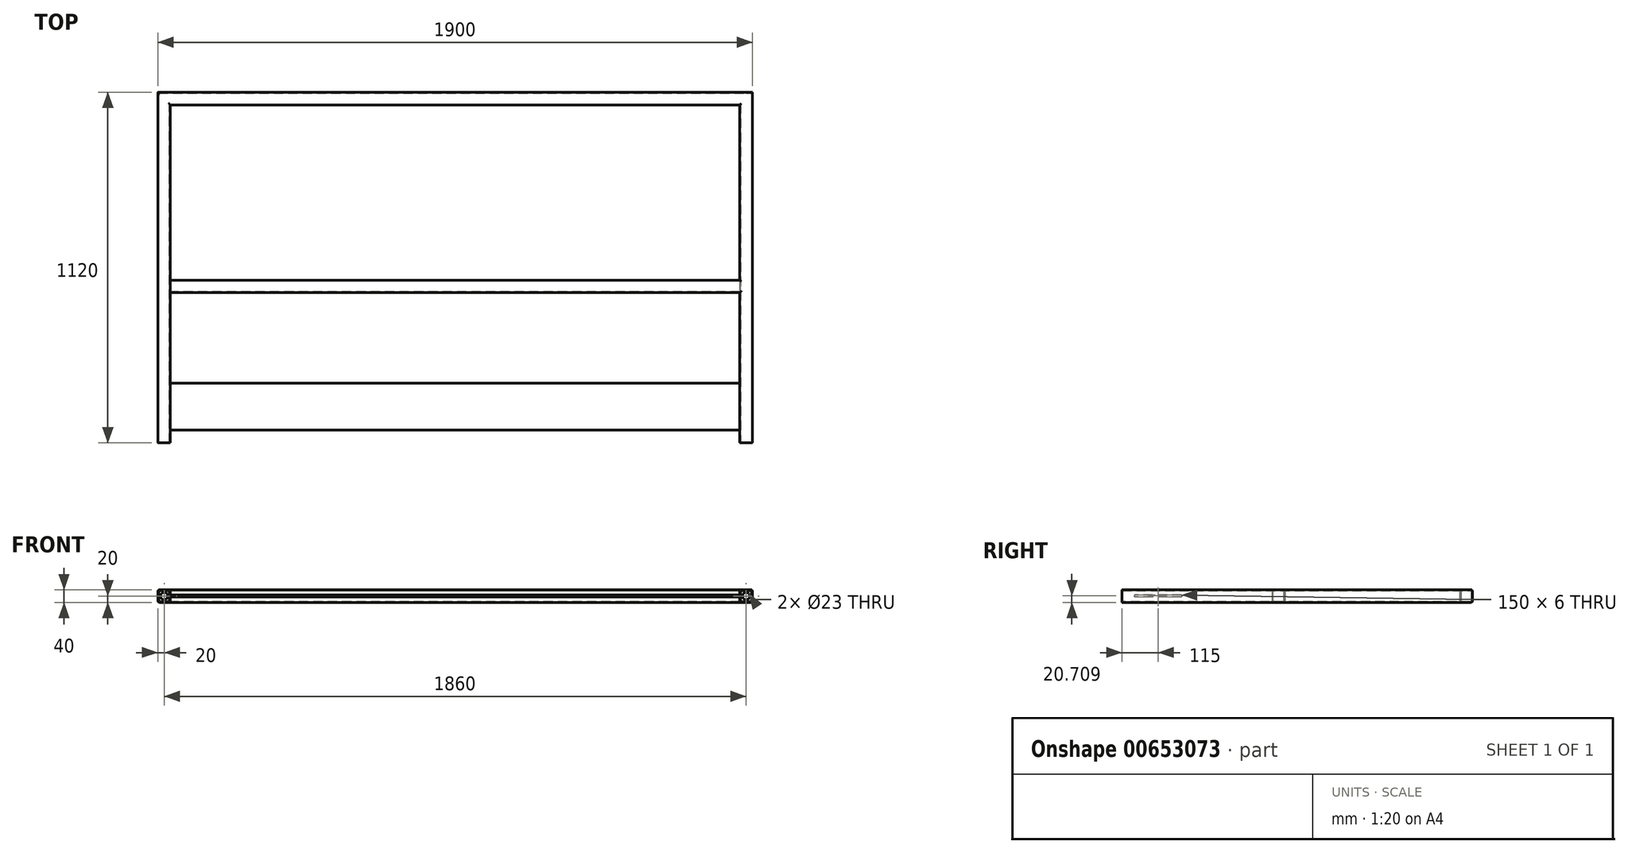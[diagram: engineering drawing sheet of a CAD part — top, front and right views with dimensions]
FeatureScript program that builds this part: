
annotation { "Feature Type Name" : "Feature", "Feature Type Description" : "" }
export const myFeature = defineFeature(function(context is Context, id is Id, definition is map)
    precondition{}
    {
        {
            var Q0;
            Q0=qCreatedBy(makeId("Front.planeOp"),FACE);
            var sketch = newSketch(context, id + "F0", { "sketchPlane" : qUnion([Q0])});
            skLineSegment(sketch, "E0.bottom", {"start": v(15, -20) * mm, "end": v(-15, -20) * mm});
            skLineSegment(sketch, "E0.top", {"start": v(15, 20) * mm, "end": v(-15, 20) * mm});
            skLineSegment(sketch, "E0.left", {"start": v(20, -15) * mm, "end": v(20, 15) * mm});
            skLineSegment(sketch, "E0.right", {"start": v(-20, -15) * mm, "end": v(-20, 15) * mm});
            skPoint(sketch, "E0.middle", {"position": v(0, 0) * mm});
            skPoint(sketch, "E1.visualSharp", {"position": v(-20, 20) * mm});
            skArc(sketch, "E1.filletArc", {"start": v(-15, 20) * mm, "mid": v(-18.54, 18.54) * mm, "end": v(-20, 15) * mm});
            skPoint(sketch, "E2.visualSharp", {"position": v(20, 20) * mm});
            skArc(sketch, "E2.filletArc", {"start": v(20, 15) * mm, "mid": v(18.54, 18.54) * mm, "end": v(15, 20) * mm});
            skPoint(sketch, "E3.visualSharp", {"position": v(20, -20) * mm});
            skArc(sketch, "E3.filletArc", {"start": v(15, -20) * mm, "mid": v(18.54, -18.54) * mm, "end": v(20, -15) * mm});
            skPoint(sketch, "E4.visualSharp", {"position": v(-20, -20) * mm});
            skArc(sketch, "E4.filletArc", {"start": v(-20, -15) * mm, "mid": v(-18.54, -18.54) * mm, "end": v(-15, -20) * mm});
            skArc(sketch, "E5.0", {"start": v(-17.5, -15) * mm, "mid": v(-16.77, -16.77) * mm, "end": v(-15, -17.5) * mm});
            skLineSegment(sketch, "E5.1", {"start": v(15, -17.5) * mm, "end": v(-15, -17.5) * mm});
            skLineSegment(sketch, "E5.2", {"start": v(-17.5, -15) * mm, "end": v(-17.5, 15) * mm});
            skArc(sketch, "E5.3", {"start": v(15, -17.5) * mm, "mid": v(16.77, -16.77) * mm, "end": v(17.5, -15) * mm});
            skArc(sketch, "E5.4", {"start": v(-15, 17.5) * mm, "mid": v(-16.77, 16.77) * mm, "end": v(-17.5, 15) * mm});
            skLineSegment(sketch, "E5.5", {"start": v(15, 17.5) * mm, "end": v(-15, 17.5) * mm});
            skArc(sketch, "E5.6", {"start": v(17.5, 15) * mm, "mid": v(16.77, 16.77) * mm, "end": v(15, 17.5) * mm});
            skLineSegment(sketch, "E5.7", {"start": v(17.5, -15) * mm, "end": v(17.5, 15) * mm});
            skSolve(sketch);
        }
        {
            var Q0;
            Q0=qCreatedBy(makeId("Top.planeOp"),FACE);
            var sketch = newSketch(context, id + "F1", { "sketchPlane" : qUnion([Q0])});
            skLineSegment(sketch, "E6.top", {"start": v(0, 1100) * mm, "end": v(1860, 1100) * mm});
            skLineSegment(sketch, "E6.left", {"start": v(0, 0) * mm, "end": v(0, 1100) * mm});
            skLineSegment(sketch, "E6.right", {"start": v(1860, 0) * mm, "end": v(1860, 1100) * mm});
            skLineSegment(sketch, "E7", {"start": v(0, 500) * mm, "end": v(1860, 500) * mm});
            skSolve(sketch);
        }
        {
            var Q0;
            Q0 = qSketchRegion(id + "F0", true);
            var Q1;
            Q1=sQuery(id+"F1.wireOp",EDGE,"E6.left");
            var Q2;
            Q2=sQuery(id+"F1.wireOp",EDGE,"E6.top");
            var Q3;
            Q3=sQuery(id+"F1.wireOp",EDGE,"E6.right");
            sweep(context, id + "F2", {"profiles" : qUnion([Q0]), "path" : qUnion([Q1, Q2, Q3])});
        }
        {
            var Q0;
            Q0=makeQuery(id+"F2.opSweep","SWEPT_FACE",FACE,{"disambiguationData":[OSD([sQuery(id+"F0.wireOp",EDGE,"E0.left"),sQuery(id+"F1.wireOp",EDGE,"E6.left")])]});
            var sketch = newSketch(context, id + "F3", { "sketchPlane" : qUnion([Q0])});
            skLineSegment(sketch, "E8.bottom", {"start": v(515, -20) * mm, "end": v(485, -20) * mm});
            skLineSegment(sketch, "E8.top", {"start": v(515, 20) * mm, "end": v(485, 20) * mm});
            skLineSegment(sketch, "E8.left", {"start": v(520, -15) * mm, "end": v(520, 15) * mm});
            skLineSegment(sketch, "E8.right", {"start": v(480, -15) * mm, "end": v(480, 15) * mm});
            skPoint(sketch, "E8.middle", {"position": v(500, 0) * mm});
            skPoint(sketch, "E9.visualSharp", {"position": v(480, 20) * mm});
            skArc(sketch, "E9.filletArc", {"start": v(485, 20) * mm, "mid": v(481.46, 18.54) * mm, "end": v(480, 15) * mm});
            skPoint(sketch, "E10.visualSharp", {"position": v(520, 20) * mm});
            skArc(sketch, "E10.filletArc", {"start": v(520, 15) * mm, "mid": v(518.54, 18.54) * mm, "end": v(515, 20) * mm});
            skPoint(sketch, "E11.visualSharp", {"position": v(520, -20) * mm});
            skArc(sketch, "E11.filletArc", {"start": v(515, -20) * mm, "mid": v(518.54, -18.54) * mm, "end": v(520, -15) * mm});
            skPoint(sketch, "E12.visualSharp", {"position": v(480, -20) * mm});
            skArc(sketch, "E12.filletArc", {"start": v(480, -15) * mm, "mid": v(481.46, -18.54) * mm, "end": v(485, -20) * mm});
            skArc(sketch, "E13.0", {"start": v(482.5, -15) * mm, "mid": v(483.23, -16.77) * mm, "end": v(485, -17.5) * mm});
            skLineSegment(sketch, "E13.1", {"start": v(515, -17.5) * mm, "end": v(485, -17.5) * mm});
            skLineSegment(sketch, "E13.2", {"start": v(482.5, -15) * mm, "end": v(482.5, 15) * mm});
            skArc(sketch, "E13.3", {"start": v(515, -17.5) * mm, "mid": v(516.77, -16.77) * mm, "end": v(517.5, -15) * mm});
            skArc(sketch, "E13.4", {"start": v(485, 17.5) * mm, "mid": v(483.23, 16.77) * mm, "end": v(482.5, 15) * mm});
            skLineSegment(sketch, "E13.5", {"start": v(515, 17.5) * mm, "end": v(485, 17.5) * mm});
            skArc(sketch, "E13.6", {"start": v(517.5, 15) * mm, "mid": v(516.77, 16.77) * mm, "end": v(515, 17.5) * mm});
            skLineSegment(sketch, "E13.7", {"start": v(517.5, -15) * mm, "end": v(517.5, 15) * mm});
            skLineSegment(sketch, "E14.0", {"start": v(1115, 20) * mm, "end": v(0, 20) * mm});
            skArc(sketch, "E15.0.0", {"start": v(1115, 20) * mm, "mid": v(1118.54, 18.54) * mm, "end": v(1120, 15) * mm});
            skLineSegment(sketch, "E15.0.1", {"start": v(1115, 20) * mm, "end": v(0, 20) * mm, "construction": true});
            skLineSegment(sketch, "E15.0.2", {"start": v(0, 15) * mm, "end": v(0, 20) * mm});
            skLineSegment(sketch, "E15.0.3", {"start": v(0, 15) * mm, "end": v(1120, 15) * mm, "construction": true});
            skSolve(sketch);
        }
        {
            var Q0;
            Q0 = qSketchRegion(id + "F3", true);
            extrude(context, id + "F4", {"entities" : qUnion([Q0]), "operationType" : NewBodyOperationType.ADD, "endBound" : BoundingType.UP_TO_NEXT, "depth" : 25 * mm, "offsetDistance" : 25 * mm});
        }
        {
            var Q0;
            {var subQ2=sQuery(id+"F3.wireOp",EDGE,"E8.right");var subQ3=sQuery(id+"F1.wireOp",EDGE,"E6.left");var subQ6=sQuery(id+"F0.wireOp",EDGE,"E0.left");Q0=makeQuery(id+"F4.boolean.opBoolean","SPLIT",FACE,{"disambiguationData":[TD([makeQuery(id+"F4.opExtrude","SWEPT_FACE",FACE,{"disambiguationData":[OSD([subQ2])]})])],"derivedFrom":makeQuery(id+"F2.opSweep","SWEPT_FACE",FACE,{"disambiguationData":[OSD([subQ6,subQ3])]})});}
            var sketch = newSketch(context, id + "F5", { "sketchPlane" : qUnion([Q0])});
            skLineSegment(sketch, "E16.bottom", {"start": v(40, -2.3) * mm, "end": v(190, -2.3) * mm});
            skLineSegment(sketch, "E16.top", {"start": v(40, 3.7) * mm, "end": v(190, 3.7) * mm});
            skLineSegment(sketch, "E16.right", {"start": v(190, -2.3) * mm, "end": v(190, 3.7) * mm});
            skLineSegment(sketch, "E17", {"start": v(40, 3.7) * mm, "end": v(40, -2.3) * mm});
            skSolve(sketch);
        }
        {
            var Q0;
            Q0 = qSketchRegion(id + "F5", true);
            extrude(context, id + "F6", {"entities" : qUnion([Q0]), "operationType" : NewBodyOperationType.ADD, "endBound" : BoundingType.UP_TO_NEXT, "depth" : 25 * mm, "offsetDistance" : 25 * mm});
        }
        {
            var Q0;
            Q0=makeQuery(id+"F2.opSweep","SWEPT_FACE",FACE,{"disambiguationData":[OSD([sQuery(id+"F0.wireOp",EDGE,"E0.right"),sQuery(id+"F1.wireOp",EDGE,"E6.top")])]});
            var sketch = newSketch(context, id + "F7", { "sketchPlane" : qUnion([Q0])});
            skLineSegment(sketch, "E18", {"start": v(-1880, 0) * mm, "end": v(20, 0) * mm, "construction": true});
            skPoint(sketch, "E19", {"position": v(0, 0) * mm});
            skPoint(sketch, "E20", {"position": v(-1860, 0) * mm});
            skSolve(sketch);
        }
        {
            var Q0;
            Q0=sQuery(id+"F7.wireOp",VERTEX,"E19");
            var Q1;
            Q1=sQuery(id+"F7.wireOp",VERTEX,"E20");
            var Q2;
            Q2=makeQuery(id+"F2.opSweep","SWEPT_BODY",BODY,{"disambiguationData":[OSD([sQuery(id+"F0.wireOp",EDGE,"E0.bottom"),sQuery(id+"F0.wireOp",EDGE,"E0.top"),sQuery(id+"F0.wireOp",EDGE,"E0.left"),sQuery(id+"F0.wireOp",EDGE,"E0.right"),sQuery(id+"F0.wireOp",EDGE,"E1.filletArc"),sQuery(id+"F0.wireOp",EDGE,"E2.filletArc"),sQuery(id+"F0.wireOp",EDGE,"E3.filletArc"),sQuery(id+"F0.wireOp",EDGE,"E4.filletArc"),sQuery(id+"F0.wireOp",EDGE,"E5.0"),sQuery(id+"F0.wireOp",EDGE,"E5.1"),sQuery(id+"F0.wireOp",EDGE,"E5.2"),sQuery(id+"F0.wireOp",EDGE,"E5.3"),sQuery(id+"F0.wireOp",EDGE,"E5.4"),sQuery(id+"F0.wireOp",EDGE,"E5.5"),sQuery(id+"F0.wireOp",EDGE,"E5.6"),sQuery(id+"F0.wireOp",EDGE,"E5.7"),sQuery(id+"F1.wireOp",EDGE,"E6.right")])]});
            hole(context, id + "F8", {"style" : HoleStyle.SIMPLE, "endStyle" : HoleEndStyle.THROUGH, "holeDiameter" : 23 * mm, "majorDiameter" : 5 * mm, "isTappedThrough" : true, "tappedDepth" : 12 * mm, "tapClearance" : 3, "locations" : qUnion([Q0, Q1]), "scope" : qUnion([Q2])});
        }
    });
